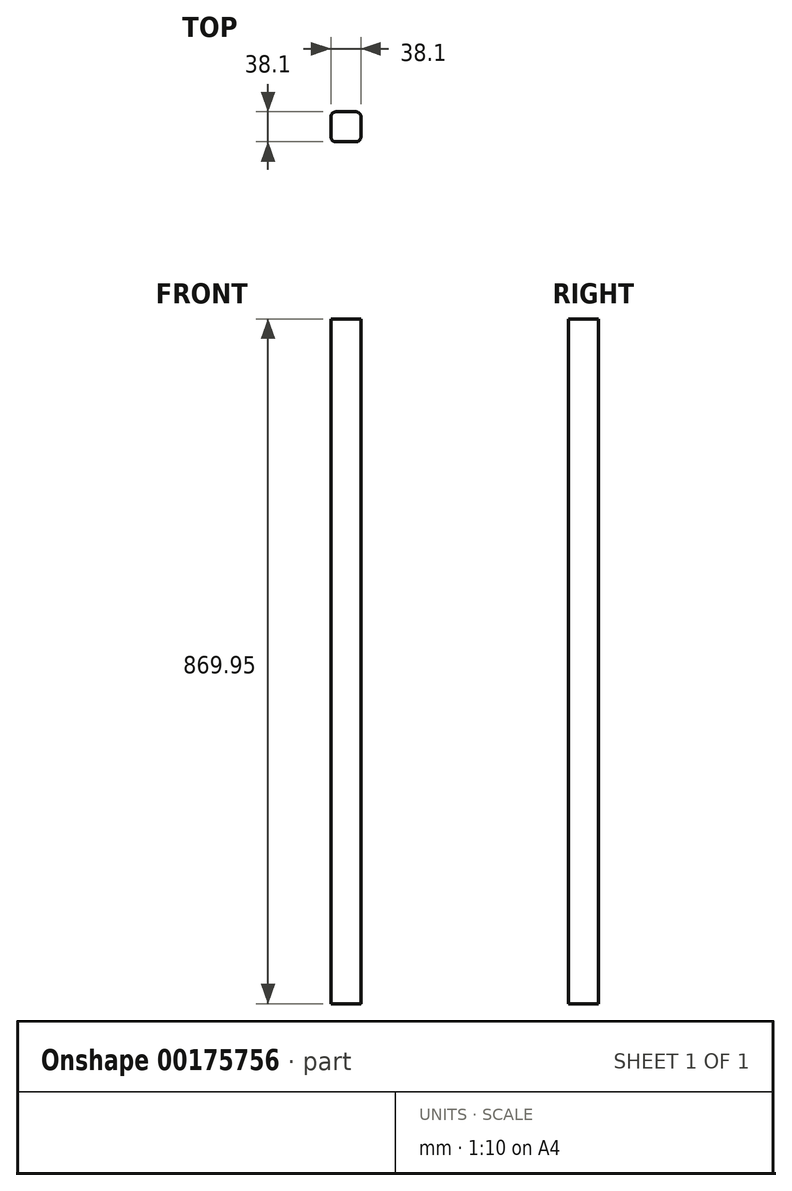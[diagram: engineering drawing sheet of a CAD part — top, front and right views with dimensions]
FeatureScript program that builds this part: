
annotation { "Feature Type Name" : "Feature", "Feature Type Description" : "" }
export const myFeature = defineFeature(function(context is Context, id is Id, definition is map)
    precondition{}
    {
        {
            var Q0;
            Q0=qCreatedBy(makeId("Top.planeOp"),FACE);
            var sketch = newSketch(context, id + "F0", { "sketchPlane" : qUnion([Q0])});
            skLineSegment(sketch, "E0.bottom", {"start": v(12.7, 19.05) * mm, "end": v(-12.7, 19.05) * mm});
            skLineSegment(sketch, "E0.top", {"start": v(12.7, -19.05) * mm, "end": v(-12.7, -19.05) * mm});
            skLineSegment(sketch, "E0.left", {"start": v(19.05, 12.7) * mm, "end": v(19.05, -12.7) * mm});
            skLineSegment(sketch, "E0.right", {"start": v(-19.05, 12.7) * mm, "end": v(-19.05, -12.7) * mm});
            skPoint(sketch, "E0.middle", {"position": v(0, 0) * mm});
            skPoint(sketch, "E1.visualSharp", {"position": v(-19.05, 19.05) * mm});
            skArc(sketch, "E1.filletArc", {"start": v(-12.7, 19.05) * mm, "mid": v(-17.2, 17.2) * mm, "end": v(-19.05, 12.7) * mm});
            skPoint(sketch, "E2.visualSharp", {"position": v(19.05, 19.05) * mm});
            skArc(sketch, "E2.filletArc", {"start": v(19.05, 12.7) * mm, "mid": v(17.2, 17.2) * mm, "end": v(12.7, 19.05) * mm});
            skPoint(sketch, "E3.visualSharp", {"position": v(19.05, -19.05) * mm});
            skArc(sketch, "E3.filletArc", {"start": v(12.7, -19.05) * mm, "mid": v(17.2, -17.2) * mm, "end": v(19.05, -12.7) * mm});
            skPoint(sketch, "E4.visualSharp", {"position": v(-19.05, -19.05) * mm});
            skArc(sketch, "E4.filletArc", {"start": v(-19.05, -12.7) * mm, "mid": v(-17.2, -17.2) * mm, "end": v(-12.7, -19.05) * mm});
            skSolve(sketch);
        }
        {
            var Q0;
            Q0=qSketchRegion(id+"F0",true);
            extrude(context, id + "F1", {"entities" : qUnion([Q0]), "depth" : 869.95 * mm, "offsetDistance" : 25.4 * mm});
        }
    });
